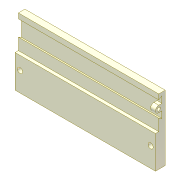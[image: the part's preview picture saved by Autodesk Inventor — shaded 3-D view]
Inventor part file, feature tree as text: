
AUTODESK INVENTOR PART (.ipt)
format: ipt  version: unknown  size: 222,208 bytes
history: native  units: in
note: dims shown in document units (in); Inventor stores cm internally (conversion verified against a paired STEP export)
features: sketch x3, extrude x3, plane x1
ambient origin geometry x8: Origin, YZ Plane, XZ Plane, XY Plane, X Axis, Y Axis, Z Axis, Center Point
feature tree (7):
  sketch  "Sketch9"  dims[d49=3.937in d50=15.748in]
  plane  "Work Plane8"
  extrude  "Extrusion9"  Depth=15.748in
  extrude  "Extrusion10"  Depth=1.9685in
  extrude  "Extrusion11"  Depth=1.9685in
  sketch  "Sketch20"  dims[d58=0.9843in d59=1.9685in]
  sketch  "Sketch21"  dims[d60=1.9685in d61=1.9685in d62=1.9685in d64=7.874in d65=7.874in d90=0.6299in d91=0.5906in d92=0.5906in d93=2.3622in d94=0.5906in d95=1.1811in d96=0.0in d97=0.3937in d98=60.0deg d99=60.0deg d100=1.1811in d101=2.3622in d102=1.5748in d103=1.5748in d104=60.0deg d105=0.3937in d106=0.3937in d107=1.1811in d108=2.3622in d109=1.1811in d110=0.0in d111=0.3937in d112=0.3937in d113=0.7874in d114=0.5906in d115=0.0in]
